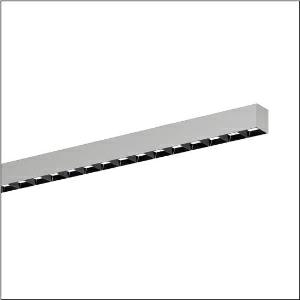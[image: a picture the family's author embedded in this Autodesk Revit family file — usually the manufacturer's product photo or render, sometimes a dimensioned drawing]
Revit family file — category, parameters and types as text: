
# Revit family: silica_r__21_51mx21tat4s_03ed
name_source: partatom
category: Lighting Fixtures
units: mm (PartAtom-declared; Revit-internal decimal feet)

## family parameters
Cut with Voids When Loaded = No
Host = Face
Light Source = No
Part Type = Normal
Room Calculation Point = No
Round Connector Dimension = Use Diameter
Shared = No

## types (1)
- --- (1 x LED, 3720 lm, 32.2 W, 6500K)
    Apparent Load = 32 VA
    CIE Flux Codes = 85 99 100 100 100
    Color Rendering = 80
    Color Temperature = 6500K
    Default Elevation = 1800 mm
    Description = Silica® 21, office luminaire, primary light control with darklight reflector, of PMMA, black, CAT 2 (L<= 3000cd/m²), light emission: direct distribution, primary light characteristic: symmetric, installation type: surface-mounted, LED, rated luminous flux: 3.720lm, luminous efficacy: 110lm/W, light colour: 8tw, colour temperature: 2700..6500K, control gear: ECG DALI, with terminal, 3+2-pole, max. 2.5mm², mains connection: 220..240V, AC, 50/60Hz, rated input power: 33.8W, luminaire housing, of aluminium, metallic grey (RAL 9006), length: 1.204mm, width: 53mm, height: 53mm, protection rating (complete): IP20, insulation class (complete): insulation class I (protective earthing), certification: CE, permissible operating ambient temperature: 0..+35°C, standard: EN 50419, packaging unit: 1 piece
    Height = 0 mm  [stored 0 ft]
    Lamp = 1 x LED
    Lamp Light Flux = 3720 lm
    Lamp Power = 32.2 W
    Lamp count = 1
    Length = 1204 mm
    Luminous efficacy = 116 lm/W
    Manufacturer = Siteco
    ModVariant = No
    Model = 51MX21TAT4S
    Mounting Place = Ceiling
    Mounting Type = Recessed
    Number of Poles = 1
    OnlyDefault = Yes
    Power Factor = 1
    Product Name = Silica® 21
    Product group = office luminaire | ceiling recessed
    ProductGroupID = 401
    Protection Class = Protection class I
    Protection Degree = IP 20
    RLX_Detail_Level = 1
    RLX_Emergency_Light_Flux = 0 lm
    RLX_Emergency_Type = 0
    RLX_Emergency_Type_DB = No
    RlxData = <blob elided: 39345 chars, md5=6a385f8c>
    Socket = socket
    Standby Power = 0 W
    System Light Flux = 3720 lm
    System Power = 32 W
    Type Comments = individual setting
    Type Image = l_1313585.jpg
    URL = http://relux.com
    VarID = @adj_089421
    Voltage = 0 V
    Weight = 0.00 kg
    Width = 53 mm

note: [stored X ft] marks values corroborated as IEEE doubles in the binary element streams (Revit-internal decimal feet)

## geometry (parser evidence)
native form markers: Blend x4, Sweep x10
no freeform markers — native parametric forms only
